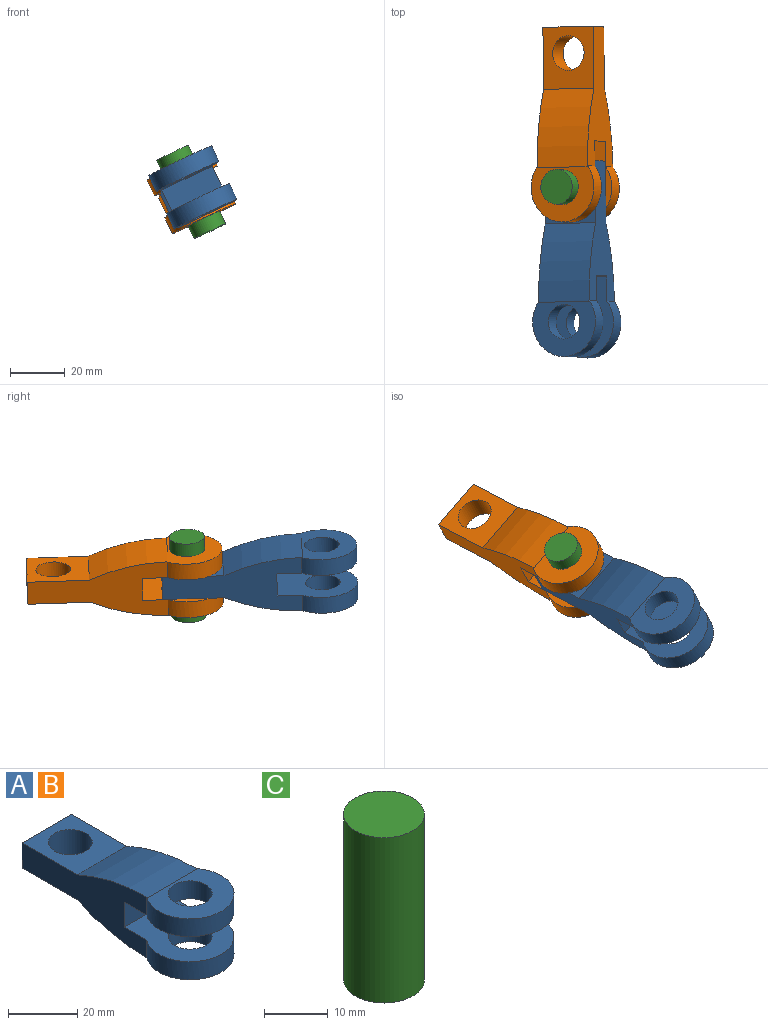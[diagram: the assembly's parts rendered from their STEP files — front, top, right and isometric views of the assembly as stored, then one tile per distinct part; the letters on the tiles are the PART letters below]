
ASSEMBLY  parts=3 mates=2
PART A: 17 faces, bbox 25.4x71.4x21.6 mm
  f0: plane 51.11x21.59mm, normal (1,0,0), area 614.5mm2, adj f2,f4,f5,f6,f8,f9,f10,f11
  f1: plane 51.11x21.59mm, normal (-1,0,0), area 614.5mm2, adj f2,f4,f5,f6,f8,f9,f10,f11
  f2: cylinder r=12.7mm len=25.4mm, axis (0,0,-1), area 357.1mm2, adj f0,f1,f3,f4,f14
  f3: plane 25.4x19.97mm, normal (0,0,1), area 300.7mm2, adj f2,f13,f14
  f4: plane 29.52x25.4mm, normal (0,0,-1), area 494.9mm2, adj f0,f1,f2,f5,f13
  f5: plane 20.32x8.89mm, normal (0,-1,0), area 180.6mm2, adj f0,f1,f4,f6
  f6: plane 29.52x25.4mm, normal (0,0,1), area 494.9mm2, adj f0,f1,f5,f11,f12
  f7: plane 25.4x19.97mm, normal (0,0,-1), area 300.7mm2, adj f11,f12,f15
  f8: plane 22.64x20.32mm, normal (0,0,-1), area 333.3mm2, adj f0,f1,f9,f15,f16
  f9: plane 20.32x8.89mm, normal (0,1,0), area 180.6mm2, adj f0,f1,f8,f10
  f10: plane 22.64x20.32mm, normal (0,0,1), area 333.3mm2, adj f0,f1,f9,f14,f16
  f11: cylinder r=12.7mm len=25.4mm, axis (0,0,-1), area 357.1mm2, adj f0,f1,f6,f7,f15
  f12: cylinder r=6.35mm len=12.7mm, axis (0,0,-1), area 253.4mm2, adj f6,f7
  f13: cylinder r=6.35mm len=12.7mm, axis (0,0,-1), area 253.4mm2, adj f3,f4
  f14: cylinder r=68.58mm len=28.82mm, axis (-1,0,0), area 604.5mm2, adj f0,f1,f2,f3,f10
  f15: cylinder r=68.58mm len=28.82mm, axis (-1,0,0), area 604.5mm2, adj f0,f1,f7,f8,f11
  f16: cylinder r=6.35mm len=12.7mm, axis (0,0,-1), area 354.7mm2, adj f8,f10
PART B: same geometry as A
PART C: 3 faces, bbox 12.7x12.7x31.8 mm
  f0: cylinder r=6.35mm len=31.75mm, axis (0,0,-1), area 1266.8mm2, adj f1,f2
  f1: plane 12.7x12.7mm, normal (0,0,1), area 126.7mm2, adj f0
  f2: plane 12.7x12.7mm, normal (0,0,-1), area 126.7mm2, adj f0
PLACE A rot(axis=(-0.07,-1,0.04),25.5deg) t=(9.55,-69.97,10.62)mm
PLACE B rot(axis=(-0.07,-1,0.04),25.5deg) t=(8.96,-20.88,9)mm
PLACE C rot(axis=(-0.07,-1,0.04),25.5deg) t=(17.69,-21.38,-9.35)mm
MATE revolute A.f16 <-> B.f12  axis (0.43,-0.02,-0.9) through (8.96,-20.88,9)mm
MATE fastened C.f0 <-> B.f2  axis (0.43,-0.02,-0.9) through (4.06,-20.6,19.32)mm
